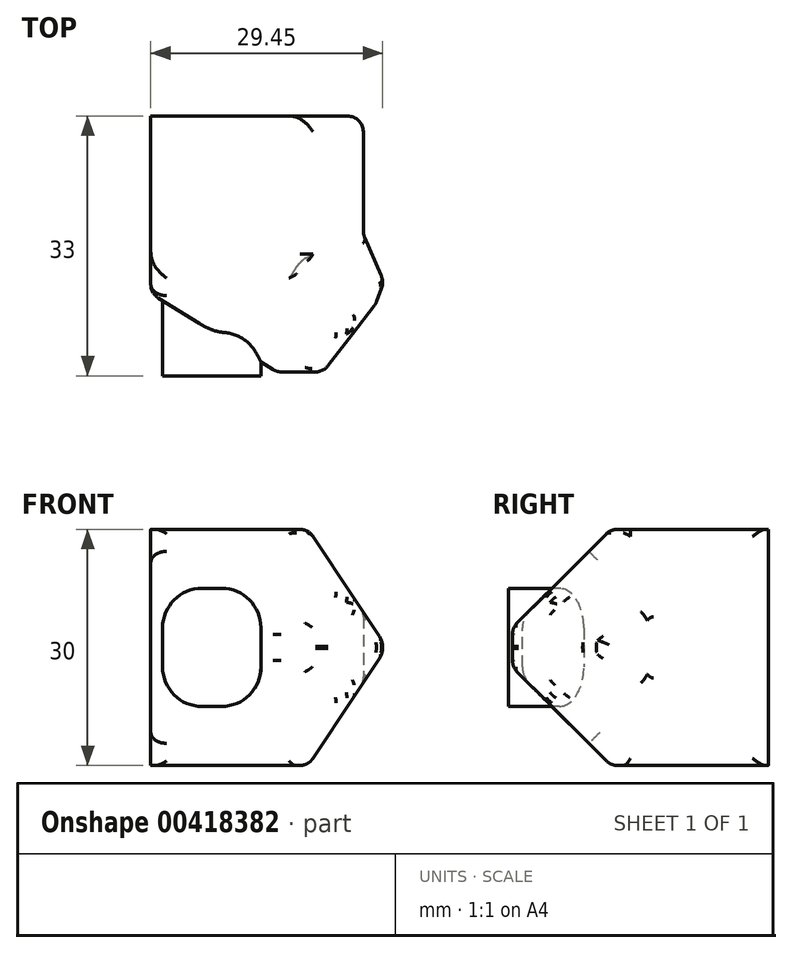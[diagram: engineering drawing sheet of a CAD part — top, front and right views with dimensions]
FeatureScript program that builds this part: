
annotation { "Feature Type Name" : "Feature", "Feature Type Description" : "" }
export const myFeature = defineFeature(function(context is Context, id is Id, definition is map)
    precondition{}
    {
        {
            var Q0;
            Q0=qCreatedBy(makeId("Top.planeOp"),FACE);
            var sketch = newSketch(context, id + "F0", { "sketchPlane" : qUnion([Q0])});
            skLineSegment(sketch, "E0", {"start": v(0, 0) * mm, "end": v(-20, 0) * mm});
            skLineSegment(sketch, "E1", {"start": v(-20, 0) * mm, "end": v(-20, -22.5) * mm});
            skLineSegment(sketch, "E2", {"start": v(-20, -22.5) * mm, "end": v(0, -35) * mm});
            skLineSegment(sketch, "E3", {"start": v(0, 0) * mm, "end": v(7, 0) * mm});
            skLineSegment(sketch, "E4", {"start": v(7, 0) * mm, "end": v(7, -15) * mm});
            skLineSegment(sketch, "E5", {"start": v(7, -15) * mm, "end": v(10, -22) * mm});
            skLineSegment(sketch, "E6", {"start": v(10, -22) * mm, "end": v(0, -35) * mm});
            skSolve(sketch);
        }
        {
            var Q0;
            Q0=qSketchRegion(id+"F0",true);
            extrude(context, id + "F1", {"entities" : qUnion([Q0]), "depth" : 15 * mm, "hasSecondDirection" : true, "secondDirectionOppositeDirection" : true, "secondDirectionDepth" : 15 * mm});
        }
        {
            var Q0;
            Q0=qCreatedBy(makeId("Front.planeOp"),FACE);
            var sketch = newSketch(context, id + "F2", { "sketchPlane" : qUnion([Q0])});
            skLineSegment(sketch, "E7.0", {"start": v(10, 15) * mm, "end": v(10, -15) * mm, "construction": true});
            skLineSegment(sketch, "E8.0", {"start": v(-20, 15) * mm, "end": v(7, 15) * mm, "construction": true});
            skLineSegment(sketch, "E9", {"start": v(10, 0) * mm, "end": v(0, 15) * mm});
            skLineSegment(sketch, "E10", {"start": v(0, 15) * mm, "end": v(10, 15) * mm});
            skLineSegment(sketch, "E11", {"start": v(10, 0) * mm, "end": v(10, 15) * mm});
            skLineSegment(sketch, "E12.MirrorCS", {"start": v(10, 0) * mm, "end": v(0, -15) * mm});
            skLineSegment(sketch, "E13.MirrorCS", {"start": v(0, -15) * mm, "end": v(10, -15) * mm});
            skLineSegment(sketch, "E14", {"start": v(10, 0) * mm, "end": v(10, -15) * mm});
            skLineSegment(sketch, "E15.0", {"start": v(7, 4.5) * mm, "end": v(7, -4.5) * mm});
            skPoint(sketch, "E16.orphan", {"position": v(7, -15) * mm});
            skSolve(sketch);
        }
        {
            var Q0;
            {var subQ3=sQuery(id+"F2.wireOp",EDGE,"E10");Q0=makeQuery(id+"F2.imprint","IMPRINT",FACE,{"disambiguationData":[TD([[makeQuery(id+"F2.imprint","IMPRINT",EDGE,{"derivedFrom":subQ3}),-1.0]])]});}
            var Q1;
            {var subQ3=sQuery(id+"F2.wireOp",EDGE,"E13.MirrorCS");Q1=makeQuery(id+"F2.imprint","IMPRINT",FACE,{"disambiguationData":[TD([[makeQuery(id+"F2.imprint","IMPRINT",EDGE,{"derivedFrom":subQ3}),1.0]])]});}
            extrude(context, id + "F3", {"entities" : qUnion([Q0, Q1]), "operationType" : NewBodyOperationType.REMOVE, "endBound" : BoundingType.THROUGH_ALL, "depth" : 25 * mm});
        }
        {
            var Q0;
            Q0=qCreatedBy(makeId("Right.planeOp"),FACE);
            var sketch = newSketch(context, id + "F4", { "sketchPlane" : qUnion([Q0])});
            skLineSegment(sketch, "E17.0", {"start": v(-35, 15) * mm, "end": v(0, 15) * mm, "construction": true});
            skLineSegment(sketch, "E18.0", {"start": v(-35, 15) * mm, "end": v(-35, -15) * mm, "construction": true});
            skLineSegment(sketch, "E19", {"start": v(-35, 0) * mm, "end": v(-20, 15) * mm});
            skLineSegment(sketch, "E20", {"start": v(-20, 15) * mm, "end": v(-35, 15) * mm});
            skLineSegment(sketch, "E21", {"start": v(-35, 0) * mm, "end": v(-35, 15) * mm});
            skLineSegment(sketch, "E22", {"start": v(-35, 0) * mm, "end": v(-35, -15) * mm});
            skLineSegment(sketch, "E23.MirrorCS", {"start": v(-35, 0) * mm, "end": v(-20, -15) * mm});
            skLineSegment(sketch, "E24", {"start": v(-20, -15) * mm, "end": v(-35, -15) * mm});
            skLineSegment(sketch, "E25", {"start": v(-32.5, 2.5) * mm, "end": v(-32.5, -2.5) * mm});
            skSolve(sketch);
        }
        {
            var Q0;
            Q0=qSketchRegion(id+"F4",true);
            extrude(context, id + "F5", {"entities" : qUnion([Q0]), "operationType" : NewBodyOperationType.REMOVE, "endBound" : BoundingType.THROUGH_ALL, "oppositeDirection" : true, "depth" : 25 * mm, "hasSecondDirection" : true, "secondDirectionBound" : SecondDirectionBoundingType.THROUGH_ALL, "secondDirectionOppositeDirection" : false, "secondDirectionDepth" : 25 * mm});
        }
        {
            var Q0;
            Q0=makeQuery(id+"F3.boolean.opBoolean","INTERSECT",EDGE,{"derivedFrom":[makeQuery(id+"F1.opExtrude","SWEPT_FACE",FACE,{"disambiguationData":[OSD([sQuery(id+"F0.wireOp",EDGE,"E6")])]}),makeQuery(id+"F3.opExtrude","SWEPT_FACE",FACE,{"disambiguationData":[OSD([sQuery(id+"F2.wireOp",EDGE,"E9")])]})]});
            var Q1;
            Q1=makeQuery(id+"F3.boolean.opBoolean","INTERSECT",EDGE,{"derivedFrom":[makeQuery(id+"F1.opExtrude","SWEPT_FACE",FACE,{"disambiguationData":[OSD([sQuery(id+"F0.wireOp",EDGE,"E6")])]}),makeQuery(id+"F3.opExtrude","SWEPT_FACE",FACE,{"disambiguationData":[OSD([sQuery(id+"F2.wireOp",EDGE,"E12.MirrorCS")])]})]});
            chamfer(context, id + "F6", {"entities" : qUnion([Q0, Q1]), "width" : 3 * mm, "tangentPropagation" : true});
        }
        {
            var Q0;
            Q0=makeQuery(id+"F5.boolean.opBoolean","INTERSECT",EDGE,{"derivedFrom":[makeQuery(id+"F3.boolean.opBoolean","COPY",FACE,{"derivedFrom":makeQuery(id+"F3.opExtrude","SWEPT_FACE",FACE,{"disambiguationData":[OSD([sQuery(id+"F2.wireOp",EDGE,"E9")])]})}),makeQuery(id+"F5.opExtrude","SWEPT_FACE",FACE,{"disambiguationData":[OSD([sQuery(id+"F4.wireOp",EDGE,"E19")])]})]});
            var Q1;
            Q1=makeQuery(id+"F5.boolean.opBoolean","INTERSECT",EDGE,{"derivedFrom":[makeQuery(id+"F3.boolean.opBoolean","COPY",FACE,{"derivedFrom":makeQuery(id+"F3.opExtrude","SWEPT_FACE",FACE,{"disambiguationData":[OSD([sQuery(id+"F2.wireOp",EDGE,"E12.MirrorCS")])]})}),makeQuery(id+"F5.opExtrude","SWEPT_FACE",FACE,{"disambiguationData":[OSD([sQuery(id+"F4.wireOp",EDGE,"E23.MirrorCS")])]})]});
            var Q2;
            Q2=makeQuery(id+"F5.boolean.opBoolean","INTERSECT",EDGE,{"derivedFrom":[makeQuery(id+"F1.opExtrude","SWEPT_FACE",FACE,{"disambiguationData":[OSD([sQuery(id+"F0.wireOp",EDGE,"E6")])]}),makeQuery(id+"F5.opExtrude","SWEPT_FACE",FACE,{"disambiguationData":[OSD([sQuery(id+"F4.wireOp",EDGE,"E19")])]})]});
            var Q3;
            Q3=makeQuery(id+"F5.boolean.opBoolean","INTERSECT",EDGE,{"derivedFrom":[makeQuery(id+"F1.opExtrude","SWEPT_FACE",FACE,{"disambiguationData":[OSD([sQuery(id+"F0.wireOp",EDGE,"E6")])]}),makeQuery(id+"F5.opExtrude","SWEPT_FACE",FACE,{"disambiguationData":[OSD([sQuery(id+"F4.wireOp",EDGE,"E23.MirrorCS")])]})]});
            chamfer(context, id + "F7", {"entities" : qUnion([Q0, Q1, Q2, Q3]), "width" : 3 * mm, "tangentPropagation" : true});
        }
        {
            var Q0;
            Q0=makeQuery(id+"F3.boolean.opBoolean","COPY",FACE,{"derivedFrom":makeQuery(id+"F3.opExtrude","SWEPT_FACE",FACE,{"disambiguationData":[OSD([sQuery(id+"F2.wireOp",EDGE,"E9")])]})});
            var Q1;
            Q1=makeQuery(id+"F1.opExtrude","SWEPT_FACE",FACE,{"disambiguationData":[OSD([sQuery(id+"F0.wireOp",EDGE,"E4")])]});
            var Q2;
            Q2=makeQuery(id+"F3.boolean.opBoolean","COPY",FACE,{"derivedFrom":makeQuery(id+"F3.opExtrude","SWEPT_FACE",FACE,{"disambiguationData":[OSD([sQuery(id+"F2.wireOp",EDGE,"E12.MirrorCS")])]})});
            var Q3;
            Q3=makeQuery(id+"F1.opExtrude","SWEPT_FACE",FACE,{"disambiguationData":[OSD([sQuery(id+"F0.wireOp",EDGE,"E5")])]});
            var Q4;
            Q4=makeQuery(id+"F6.opChamfer","BLEND_FACE",FACE,{"disambiguationData":[OSD([sQuery(id+"F0.wireOp",EDGE,"E6"),sQuery(id+"F2.wireOp",EDGE,"E12.MirrorCS")])]});
            var Q5;
            Q5=makeQuery(id+"F6.opChamfer","BLEND_FACE",FACE,{"disambiguationData":[OSD([sQuery(id+"F0.wireOp",EDGE,"E6"),sQuery(id+"F2.wireOp",EDGE,"E9")])]});
            var Q6;
            Q6=makeQuery(id+"F1.opExtrude","SWEPT_FACE",FACE,{"disambiguationData":[OSD([sQuery(id+"F0.wireOp",EDGE,"E6")])]});
            var Q7;
            Q7=makeQuery(id+"F7.opChamfer","BLEND_FACE",FACE,{"disambiguationData":[OSD([sQuery(id+"F0.wireOp",EDGE,"E6"),sQuery(id+"F4.wireOp",EDGE,"E23.MirrorCS")])]});
            var Q8;
            Q8=makeQuery(id+"F7.opChamfer","BLEND_FACE",FACE,{"disambiguationData":[OSD([sQuery(id+"F0.wireOp",EDGE,"E6"),sQuery(id+"F4.wireOp",EDGE,"E19")])]});
            var Q9;
            Q9=makeQuery(id+"F7.opChamfer","BLEND_FACE",FACE,{"disambiguationData":[OSD([sQuery(id+"F2.wireOp",EDGE,"E9"),sQuery(id+"F4.wireOp",EDGE,"E19")])]});
            var Q10;
            {var subQ0=makeQuery(id+"F5.opExtrude","SWEPT_FACE",FACE,{"disambiguationData":[OSD([sQuery(id+"F4.wireOp",EDGE,"E23.MirrorCS")])]});Q10=makeQuery(id+"F7.opChamfer","BLEND_EDGE",EDGE,{"blendedFrom":[makeQuery(id+"F5.boolean.opBoolean","INTERSECT",EDGE,{"derivedFrom":[makeQuery(id+"F3.boolean.opBoolean","COPY",FACE,{"derivedFrom":makeQuery(id+"F3.opExtrude","SWEPT_FACE",FACE,{"disambiguationData":[OSD([sQuery(id+"F2.wireOp",EDGE,"E12.MirrorCS")])]})}),subQ0]}),makeQuery(id+"F5.boolean.opBoolean","COPY",FACE,{"derivedFrom":subQ0})],"blendedInto":[makeQuery(id+"F5.boolean.opBoolean","COPY",FACE,{"derivedFrom":subQ0})]});}
            var Q11;
            Q11=makeQuery(id+"F5.boolean.opBoolean","COPY",FACE,{"derivedFrom":makeQuery(id+"F5.opExtrude","SWEPT_FACE",FACE,{"disambiguationData":[OSD([sQuery(id+"F4.wireOp",EDGE,"E19")])]})});
            var Q12;
            Q12=makeQuery(id+"F5.boolean.opBoolean","COPY",FACE,{"derivedFrom":makeQuery(id+"F5.opExtrude","SWEPT_FACE",FACE,{"disambiguationData":[OSD([sQuery(id+"F4.wireOp",EDGE,"E23.MirrorCS")])]})});
            var Q13;
            Q13=makeQuery(id+"F1.opExtrude","SWEPT_FACE",FACE,{"disambiguationData":[OSD([sQuery(id+"F0.wireOp",EDGE,"E2")])]});
            fillet(context, id + "F8", {"entities" : qUnion([Q0, Q1, Q2, Q3, Q4, Q5, Q6, Q7, Q8, Q9, Q10, Q11, Q12, Q13]), "radius" : 2 * mm, "tangentPropagation" : true, "allowEdgeOverflow" : false});
        }
        {
            var Q0;
            Q0=qCreatedBy(makeId("Top.planeOp"),FACE);
            var sketch = newSketch(context, id + "F9", { "sketchPlane" : qUnion([Q0])});
            skLineSegment(sketch, "E26", {"start": v(-6, -18) * mm, "end": v(-18.5, -18) * mm});
            skLineSegment(sketch, "E27", {"start": v(-18.5, -18) * mm, "end": v(-18.5, -33) * mm});
            skLineSegment(sketch, "E28", {"start": v(-18.5, -33) * mm, "end": v(-6, -33) * mm});
            skLineSegment(sketch, "E29", {"start": v(-6, -33) * mm, "end": v(-6, -18) * mm});
            skSolve(sketch);
        }
        {
            var Q0;
            Q0=qSketchRegion(id+"F9",true);
            extrude(context, id + "F10", {"entities" : qUnion([Q0]), "operationType" : NewBodyOperationType.ADD, "depth" : 7.5 * mm, "hasSecondDirection" : true, "secondDirectionOppositeDirection" : true, "secondDirectionDepth" : 7.5 * mm});
        }
        {
            var Q0;
            Q0=makeQuery(id+"F10.opExtrude","CAP_EDGE",EDGE,{"disambiguationData":[OSD([sQuery(id+"F9.wireOp",EDGE,"E27")])],"isStart":false});
            var Q1;
            Q1=makeQuery(id+"F10.opExtrude","CAP_EDGE",EDGE,{"disambiguationData":[OSD([sQuery(id+"F9.wireOp",EDGE,"E27")])],"isStart":true});
            var Q2;
            Q2=makeQuery(id+"F10.opExtrude","CAP_EDGE",EDGE,{"disambiguationData":[OSD([sQuery(id+"F9.wireOp",EDGE,"E29")])],"isStart":false});
            var Q3;
            Q3=makeQuery(id+"F10.opExtrude","CAP_EDGE",EDGE,{"disambiguationData":[OSD([sQuery(id+"F9.wireOp",EDGE,"E29")])],"isStart":true});
            fillet(context, id + "F11", {"entities" : qUnion([Q0, Q1, Q2, Q3]), "radius" : 5 * mm, "tangentPropagation" : true, "allowEdgeOverflow" : false});
        }
    });
